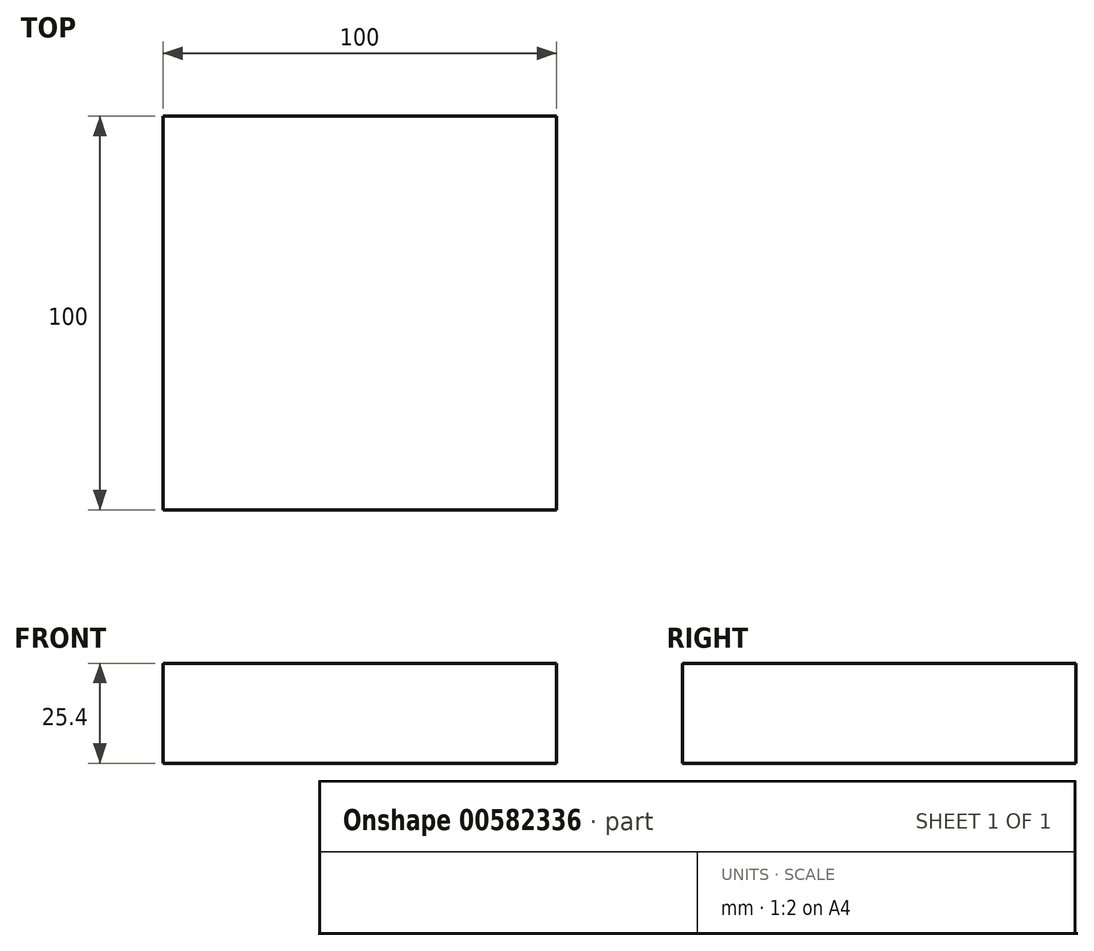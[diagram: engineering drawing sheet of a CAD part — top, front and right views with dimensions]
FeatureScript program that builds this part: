
annotation { "Feature Type Name" : "Feature", "Feature Type Description" : "" }
export const myFeature = defineFeature(function(context is Context, id is Id, definition is map)
    precondition{}
    {
        {
            var Q0;
            Q0=qCreatedBy(makeId("Top.planeOp"),FACE);
            var sketch = newSketch(context, id + "F0", { "sketchPlane" : qUnion([Q0])});
            skLineSegment(sketch, "E0.bottom", {"start": v(0, 0) * mm, "end": v(-100, 0) * mm});
            skLineSegment(sketch, "E0.top", {"start": v(0, -100) * mm, "end": v(-100, -100) * mm});
            skLineSegment(sketch, "E0.left", {"start": v(0, 0) * mm, "end": v(0, -100) * mm});
            skLineSegment(sketch, "E0.right", {"start": v(-100, 0) * mm, "end": v(-100, -100) * mm});
            skSolve(sketch);
        }
        {
            var Q0;
            Q0=makeQuery(id+"F0.imprint","IMPRINT",FACE,{"disambiguationData":[TD([[makeQuery(id+"F0.imprint","IMPRINT",EDGE,{"derivedFrom":sQuery(id+"F0.wireOp",EDGE,"E0.bottom")}),1.0]])]});
            extrude(context, id + "F1", {"entities" : qUnion([Q0]), "depth" : 25.4 * mm, "offsetDistance" : 25.4 * mm});
        }
    });
